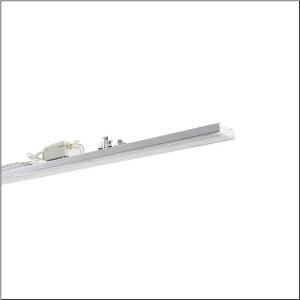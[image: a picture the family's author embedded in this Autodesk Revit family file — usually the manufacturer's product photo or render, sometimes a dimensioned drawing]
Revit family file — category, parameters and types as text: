
# Revit family: licross_r__21_recessed_mo_52tl1emn4a5g_a556
name_source: partatom
category: Lighting Fixtures
units: mm (PartAtom-declared; Revit-internal decimal feet)

## family parameters
Cut with Voids When Loaded = No
Host = Face
Light Source = No
Part Type = Normal
Room Calculation Point = No
Round Connector Dimension = Use Diameter
Shared = No

## types (1)
- --- (1 x LED, 10630 lm, 60.5 W, 4000K)
    Apparent Load = 61 VA
    CIE Flux Codes = 85 95 99 100 100
    Color Rendering = 80
    Color Temperature = 4000K
    Default Elevation = 1800 mm
    Description = Licross® 21 Recessed MO, luminaire insert, of sheet steel, galvanised, coil coated, white, length: 1.500mm, width: 66mm, height: 67mm, LED rated luminous flux: 10.630lm, light colour: 840, control gear: ON/OFF Multilumen, with plug, 3-pole, with phase selection, mains connection: 220..240V, AC, 50/60Hz, rated input power: 61W, halogen-free wiring, primary light control with lens, of plastic, primary optical cover: cover, of PMMA, light emission: direct distribution, primary light characteristic: symmetric, protection rating (complete): IP40, insulation class (complete): insulation class I (protective earthing), certification: CE, ENEC, VDE, UKCA, protection symbol: D if used in an environment without relevant dust loads with corresponding accessories, impact resistance: IK06, permissible ambient temperature for indoor applications: -35..+40°C, corresponds to IFS (International Featured Standards) requirements for safety and quality in the food industry, reducing of maximum allowable ambient temperature of 5°C with ceiling mounting, LABS conformity tested according to VDMA 24364:2018-05, packaging unit: 1 piece
    Height = 58 mm
    Lamp = 1 x LED
    Lamp Light Flux = 10630 lm
    Lamp Power = 60.5 W
    Lamp count = 1
    Length = 1500 mm
    Luminous efficacy = 176 lm/W
    Manufacturer = Siteco
    ModVariant = No
    Model = 52TL1EMN4A5G
    Mounting Place = Ceiling
    Mounting Type = Pendant
    Number of Poles = 1
    OnlyDefault = Yes
    Power Factor = 1
    Product Name = Licross® 21 Recessed MO
    Product group = luminaire insert
    ProductGroupID = 901
    Protection Class = Protection class I
    Protection Degree = IP 40
    RLX_Detail_Level = 1
    RLX_Emergency_Light_Flux = 0 lm
    RLX_Emergency_Type = 0
    RLX_Emergency_Type_DB = No
    RlxData = <blob elided: 22309 chars, md5=3d604a5a>
    Socket = socket
    Standby Power = 0 W
    System Light Flux = 10630 lm
    System Power = 61 W
    Type Comments = factory setting: luminous flux: 100 % | (A | C | E) | 140 mA
    Type Image = l_1296930.jpg
    URL = http://relux.com
    VarID = @adj_036637
    Voltage = 0 V
    Weight = 0.00 kg
    Width = 66 mm

## geometry (parser evidence)
native form markers: Blend x4, Sweep x12
no freeform markers — native parametric forms only
